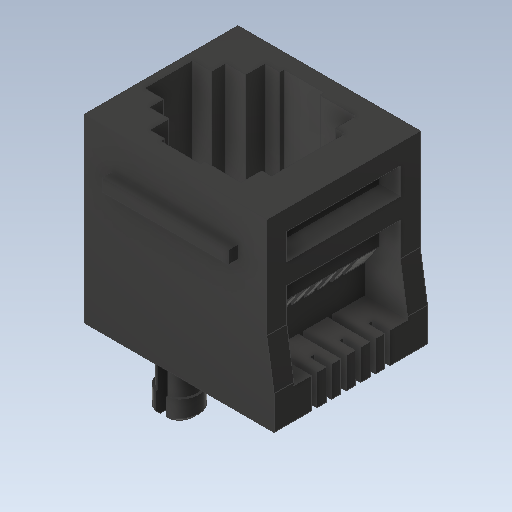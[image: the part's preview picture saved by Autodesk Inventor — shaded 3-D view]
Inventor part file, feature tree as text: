
AUTODESK INVENTOR PART (.ipt)
format: ipt  version: 2020 (Build 240168000, 168)  size: 442,368 bytes
history: native  units: in
note: dims shown in document units (in); Inventor stores cm internally (conversion verified against a paired STEP export)
features: sketch x13, extrude x11, plane x2, revolve x2, projected_geometry x1
ambient origin geometry x8: Origin, YZ Plane, XZ Plane, XY Plane, X Axis, Y Axis, Z Axis, Center Point
bodies: Solid1 (feature_tree)
feature tree (29):
  extrude  "Extrusion1"  Depth=0.526in
  extrude  "Extrusion2"  Depth=0.65in
  extrude  "Extrusion3"  Depth=0.346in
  extrude  "Extrusion4"  Depth=0.025in
  extrude  "Extrusion5"  Depth=0.12in
  extrude  "Extrusion6"  Depth=0.125in
  plane  "Work Plane1"
  plane  "Work Plane2"
  revolve  "Revolution1"  [1 undecoded]
  revolve  "Revolution2"  [1 undecoded]
  extrude  "Extrusion7"  Depth=0.051in
  extrude  "Extrusion8"  Depth=0.1315in
  extrude  "Extrusion9"  Depth=0.55in
  extrude  "Extrusion10"  Depth=0.298in
  extrude  "Extrusion11"  Depth=0.02in
  sketch  "Sketch1"  dims[d0=0.625in d1=0.526in]
  sketch  "Sketch2"  dims[d2=0.62in d3=0.0in d4=0.65in]
  sketch  "Sketch3"  dims[d5=0.115in d6=0.346in]
  sketch  "Sketch4"  dims[d7=0.62in d8=0.0in d9=0.025in]
  sketch  "Sketch5"  dims[d10=0.083in d11=0.12in]
  sketch  "Sketch6"  dims[d12=0.033in d13=0.125in]
  sketch  "Sketch7"  dims[d14=0.1265in d15=0.198in]
  sketch  "Sketch8"  dims[d16=0.2125in d17=0.065in]
  sketch  "Sketch9"  dims[d18=0.068in d19=0.051in]
  sketch  "Sketch10"  dims[d20=0.138in d21=0.1315in]
  sketch  "Sketch11"  dims[d22=0.55in d23=0.0in d24=0.044in]
  sketch  "Sketch12"  dims[d25=0.122in d27=0.298in]
  projected_geometry  "Projected Loop1"
  sketch  "Sketch13"  dims[d28=0.43in d29=0.0in d30=0.02in d31=0.27in d32=0.15in d34=2.3622in d36=0.04in d37=0.3937in d39=1.0in d41=0.197in d42=0.43in d43=0.0in d44=0.146in d45=0.073in d46=0.0725in d47=0.073in d48=0.05in d49=0.0in d50=0.1938in d51=-0.1938in d52=0.06in d53=0.196in d54=0.066in d55=45.0deg d56=0.05in d57=0.16in d58=0.086in d59=90.0deg d60=0.06in d61=0.196in d62=0.066in d63=45.0deg d64=0.05in d66=0.086in d67=90.0deg d68=0.036in d69=0.1in d70=0.0in d71=0.07in d72=0.09in d73=0.07in d74=0.115in d75=0.071in d76=0.105in d77=0.158in d78=0.08in d79=0.0725in d80=0.389in d81=0.0in d82=0.018in d83=0.129in d84=0.161in d85=1.1811in d87=0.1in d88=0.3937in d90=1.0in d92=0.05in d93=0.058in d94=1.1811in d96=0.1in d97=0.3937in d99=1.0in d101=0.389in d102=0.0in d103=0.02in d105=0.07in d106=2.3622in d108=0.0452in d109=0.3937in d111=1.0in d113=0.389in d114=0.0in d115=0.025in d116=0.4in d117=0.0in]
note: 2 required parameter values undecoded (feature->parameter linkage not recoverable at this tier; creation-order binding heuristic only, values carry confidence <= 0.55)
